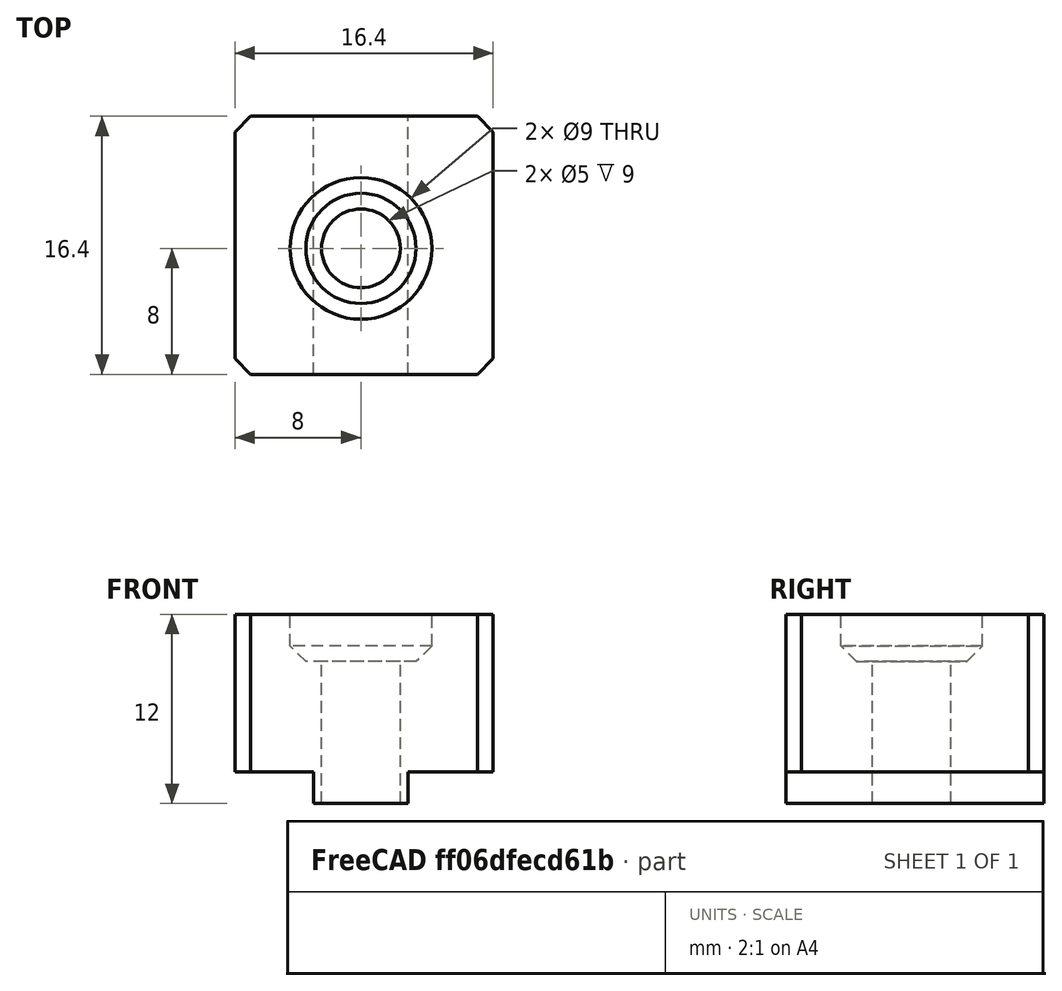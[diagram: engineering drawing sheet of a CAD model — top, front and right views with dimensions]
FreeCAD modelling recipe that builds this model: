
FCSTD DOCUMENT  (FreeCAD 0.18R)
Label: caja electronica
License: All rights reserved
LicenseURL: http://en.wikipedia.org/wiki/All_rights_reserved
objects: Part::Box×2, Part::Cylinder×2, Part::Cut×2, Part::Chamfer×2, Part::MultiFuse×1, Part::Feature×1
note: 10 computed .brp shape members not serialized (recipe doc carries the construction recipe); baked Part::Feature solids carry a one-line shape summary decoded from their .brp

FEATURE [Part::Box] Box  label="Cubo"
  AttacherType = Attacher::AttachEngine3D
  Height = 10
  Length = 16.4
  Width = 16.4
FEATURE [Part::Box] Box001  label="Cubo001"
  AttacherType = Attacher::AttachEngine3D
  Height = 6
  Length = 6
  Placement = pos=(5,0,-2) rot=(0,0,1;0rad)
  Width = 16.4
FEATURE [Part::MultiFuse] Fusion
  Shapes = -> [Box,Box001]
FEATURE [Part::Cylinder] Cylinder  label="Cilindro"
  Angle = 360
  AttacherType = Attacher::AttachEngine3D
  Height = 20
  Placement = pos=(8,8,-8) rot=(0,0,1;0rad)
  Radius = 2.5
FEATURE [Part::Cut] Cut
  Base = -> Fusion
  Tool = -> Cylinder
FEATURE [Part::Cylinder] Cylinder001  label="Cilindro001"
  Angle = 360
  AttacherType = Attacher::AttachEngine3D
  Height = 10
  Radius = 4.5
FEATURE [Part::Chamfer] Chamfer
  Base = -> Cylinder001
  Edges = 1 edges r=1: [Edge3]
  Placement = pos=(8,8,7) rot=(0,0,1;0rad)
FEATURE [Part::Cut] Cut001
  Base = -> Cut
  Tool = -> Chamfer
FEATURE [Part::Chamfer] Chamfer001
  Base = -> Cut001
  Edges = 4 edges r=1: [Edge1,Edge3,Edge10,Edge20]
FEATURE [Part::Feature] Chamfer001001  label="Chamfer002"
  shape: bbox 16.4 x 16.4 x 12 mm, 18 faces (baked)
